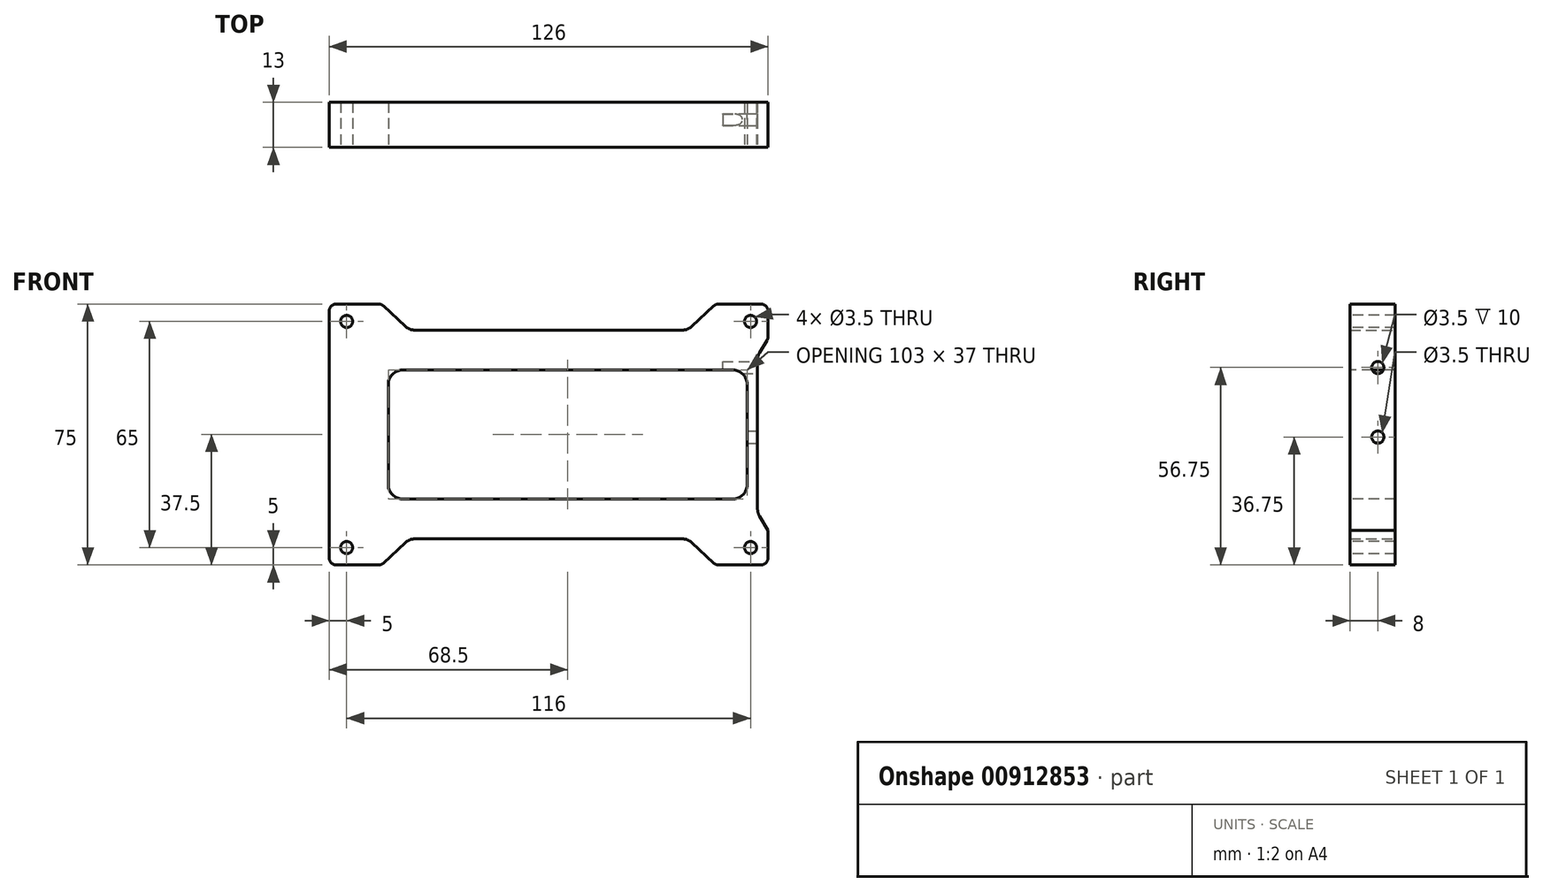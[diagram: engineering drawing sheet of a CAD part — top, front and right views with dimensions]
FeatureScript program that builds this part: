
annotation { "Feature Type Name" : "Feature", "Feature Type Description" : "" }
export const myFeature = defineFeature(function(context is Context, id is Id, definition is map)
    precondition{}
    {
        {
            var Q0;
            Q0=qCreatedBy(makeId("Front.planeOp"),FACE);
            var sketch = newSketch(context, id + "F0", { "sketchPlane" : qUnion([Q0])});
            skLineSegment(sketch, "E0.bottom", {"start": v(0, 0) * mm, "end": v(15, 0) * mm});
            skLineSegment(sketch, "E0.top", {"start": v(0, 75) * mm, "end": v(15, 75) * mm});
            skLineSegment(sketch, "E0.left", {"start": v(0, 0) * mm, "end": v(0, 75) * mm});
            skLineSegment(sketch, "E0.right", {"start": v(126, 0) * mm, "end": v(126, 75) * mm});
            skLineSegment(sketch, "E1", {"start": v(23, 67.5) * mm, "end": v(103, 67.5) * mm});
            skLineSegment(sketch, "E2", {"start": v(23, 7.5) * mm, "end": v(103, 7.5) * mm});
            skLineSegment(sketch, "E3", {"start": v(23, 7.5) * mm, "end": v(15, 0) * mm});
            skLineSegment(sketch, "E4", {"start": v(103, 7.5) * mm, "end": v(111, 0) * mm});
            skLineSegment(sketch, "E5", {"start": v(23, 67.5) * mm, "end": v(15, 75) * mm});
            skLineSegment(sketch, "E6", {"start": v(103, 67.5) * mm, "end": v(111, 75) * mm});
            skLineSegment(sketch, "E7.trimOffspring", {"start": v(111, 75) * mm, "end": v(126, 75) * mm});
            skLineSegment(sketch, "E8.trimOffspring", {"start": v(111, 0) * mm, "end": v(126, 0) * mm});
            skSolve(sketch);
        }
        {
            var Q0;
            Q0 = qSketchRegion(id + "F0", true);
            extrude(context, id + "F1", {"entities" : qUnion([Q0]), "depth" : 13 * mm, "offsetDistance" : 25 * mm});
        }
        {
            var Q0;
            Q0=makeQuery(id+"F1.opExtrude","CAP_FACE",FACE,{"disambiguationData":[OSD([sQuery(id+"F0.wireOp",EDGE,"E0.bottom"),sQuery(id+"F0.wireOp",EDGE,"E0.top"),sQuery(id+"F0.wireOp",EDGE,"E0.left"),sQuery(id+"F0.wireOp",EDGE,"E0.right"),sQuery(id+"F0.wireOp",EDGE,"E1"),sQuery(id+"F0.wireOp",EDGE,"E2"),sQuery(id+"F0.wireOp",EDGE,"E3"),sQuery(id+"F0.wireOp",EDGE,"E4"),sQuery(id+"F0.wireOp",EDGE,"E5"),sQuery(id+"F0.wireOp",EDGE,"E6"),sQuery(id+"F0.wireOp",EDGE,"E7.trimOffspring"),sQuery(id+"F0.wireOp",EDGE,"E8.trimOffspring")])],"isStart":false});
            var sketch = newSketch(context, id + "F2", { "sketchPlane" : qUnion([Q0])});
            skLineSegment(sketch, "E9.bottom", {"start": v(21, 56) * mm, "end": v(116, 56) * mm});
            skLineSegment(sketch, "E9.top", {"start": v(21, 19) * mm, "end": v(116, 19) * mm});
            skLineSegment(sketch, "E9.left", {"start": v(17, 52) * mm, "end": v(17, 23) * mm});
            skLineSegment(sketch, "E9.right", {"start": v(120, 52) * mm, "end": v(120, 23) * mm});
            skPoint(sketch, "E10.visualSharp", {"position": v(17, 56) * mm});
            skArc(sketch, "E10.filletArc", {"start": v(21, 56) * mm, "mid": v(18.17, 54.83) * mm, "end": v(17, 52) * mm});
            skPoint(sketch, "E11.visualSharp", {"position": v(120, 56) * mm});
            skArc(sketch, "E11.filletArc", {"start": v(120, 52) * mm, "mid": v(118.83, 54.83) * mm, "end": v(116, 56) * mm});
            skPoint(sketch, "E12.visualSharp", {"position": v(120, 19) * mm});
            skArc(sketch, "E12.filletArc", {"start": v(116, 19) * mm, "mid": v(118.83, 20.17) * mm, "end": v(120, 23) * mm});
            skPoint(sketch, "E13.visualSharp", {"position": v(17, 19) * mm});
            skArc(sketch, "E13.filletArc", {"start": v(17, 23) * mm, "mid": v(18.17, 20.17) * mm, "end": v(21, 19) * mm});
            skSolve(sketch);
        }
        {
            var Q0;
            Q0 = qSketchRegion(id + "F2", true);
            extrude(context, id + "F3", {"entities" : qUnion([Q0]), "operationType" : NewBodyOperationType.REMOVE, "oppositeDirection" : true, "depth" : 25 * mm, "offsetDistance" : 25 * mm});
        }
        {
            var Q0;
            Q0=makeQuery(id+"F1.opExtrude","CAP_FACE",FACE,{"disambiguationData":[OSD([sQuery(id+"F0.wireOp",EDGE,"E0.bottom"),sQuery(id+"F0.wireOp",EDGE,"E0.top"),sQuery(id+"F0.wireOp",EDGE,"E0.left"),sQuery(id+"F0.wireOp",EDGE,"E0.right"),sQuery(id+"F0.wireOp",EDGE,"E1"),sQuery(id+"F0.wireOp",EDGE,"E2"),sQuery(id+"F0.wireOp",EDGE,"E3"),sQuery(id+"F0.wireOp",EDGE,"E4"),sQuery(id+"F0.wireOp",EDGE,"E5"),sQuery(id+"F0.wireOp",EDGE,"E6"),sQuery(id+"F0.wireOp",EDGE,"E7.trimOffspring"),sQuery(id+"F0.wireOp",EDGE,"E8.trimOffspring")])],"isStart":false});
            var sketch = newSketch(context, id + "F4", { "sketchPlane" : qUnion([Q0])});
            skLineSegment(sketch, "E14", {"start": v(123, 60) * mm, "end": v(123, 15) * mm});
            skLineSegment(sketch, "E15", {"start": v(123, 60) * mm, "end": v(126, 65) * mm});
            skLineSegment(sketch, "E16", {"start": v(123, 15) * mm, "end": v(126, 10) * mm});
            skLineSegment(sketch, "E17", {"start": v(126, 65) * mm, "end": v(126, 10) * mm});
            skSolve(sketch);
        }
        {
            var Q0;
            Q0 = qSketchRegion(id + "F4", true);
            extrude(context, id + "F5", {"entities" : qUnion([Q0]), "operationType" : NewBodyOperationType.REMOVE, "oppositeDirection" : true, "depth" : 25 * mm, "offsetDistance" : 25 * mm});
        }
        {
            var Q0;
            Q0=makeQuery(id+"F5.boolean.opBoolean","COPY",FACE,{"derivedFrom":makeQuery(id+"F5.opExtrude","SWEPT_FACE",FACE,{"disambiguationData":[OSD([sQuery(id+"F4.wireOp",EDGE,"E14")])]})});
            var sketch = newSketch(context, id + "F6", { "sketchPlane" : qUnion([Q0])});
            skCircle(sketch, "E18", {"center": v(-5, 36.75) * mm, "radius": 1.75 * mm});
            skCircle(sketch, "E19", {"center": v(-5, 56.75) * mm, "radius": 1.75 * mm});
            skSolve(sketch);
        }
        {
            var Q0;
            Q0 = qSketchRegion(id + "F6", true);
            extrude(context, id + "F7", {"entities" : qUnion([Q0]), "operationType" : NewBodyOperationType.REMOVE, "oppositeDirection" : true, "depth" : 10 * mm, "offsetDistance" : 25 * mm});
        }
        {
            var Q0;
            Q0=makeQuery(id+"F1.opExtrude","CAP_FACE",FACE,{"disambiguationData":[OSD([sQuery(id+"F0.wireOp",EDGE,"E0.bottom"),sQuery(id+"F0.wireOp",EDGE,"E0.top"),sQuery(id+"F0.wireOp",EDGE,"E0.left"),sQuery(id+"F0.wireOp",EDGE,"E0.right"),sQuery(id+"F0.wireOp",EDGE,"E1"),sQuery(id+"F0.wireOp",EDGE,"E2"),sQuery(id+"F0.wireOp",EDGE,"E3"),sQuery(id+"F0.wireOp",EDGE,"E4"),sQuery(id+"F0.wireOp",EDGE,"E5"),sQuery(id+"F0.wireOp",EDGE,"E6"),sQuery(id+"F0.wireOp",EDGE,"E7.trimOffspring"),sQuery(id+"F0.wireOp",EDGE,"E8.trimOffspring")])],"isStart":false});
            var sketch = newSketch(context, id + "F8", { "sketchPlane" : qUnion([Q0])});
            skCircle(sketch, "E20", {"center": v(5, 70) * mm, "radius": 1.75 * mm});
            skCircle(sketch, "E21", {"center": v(5, 5) * mm, "radius": 1.75 * mm});
            skCircle(sketch, "E22", {"center": v(121, 5) * mm, "radius": 1.75 * mm});
            skCircle(sketch, "E23", {"center": v(121, 70) * mm, "radius": 1.75 * mm});
            skSolve(sketch);
        }
        {
            var Q0;
            Q0 = qSketchRegion(id + "F8", true);
            extrude(context, id + "F9", {"entities" : qUnion([Q0]), "operationType" : NewBodyOperationType.REMOVE, "oppositeDirection" : true, "depth" : 25 * mm, "offsetDistance" : 25 * mm});
        }
        {
            var Q0;
            Q0=makeQuery(id+"F1.opExtrude","SWEPT_EDGE",EDGE,{"disambiguationData":[OSD([sQuery(id+"F0.wireOp",EDGE,"E2"),sQuery(id+"F0.wireOp",EDGE,"E3")])]});
            var Q1;
            Q1=makeQuery(id+"F1.opExtrude","SWEPT_EDGE",EDGE,{"disambiguationData":[OSD([sQuery(id+"F0.wireOp",EDGE,"E2"),sQuery(id+"F0.wireOp",EDGE,"E4")])]});
            var Q2;
            Q2=makeQuery(id+"F5.boolean.opBoolean","COPY",EDGE,{"derivedFrom":makeQuery(id+"F5.opExtrude","SWEPT_EDGE",EDGE,{"disambiguationData":[OSD([sQuery(id+"F4.wireOp",EDGE,"E14"),sQuery(id+"F4.wireOp",EDGE,"E16")])]})});
            var Q3;
            Q3=makeQuery(id+"F5.boolean.opBoolean","COPY",EDGE,{"derivedFrom":makeQuery(id+"F5.opExtrude","SWEPT_EDGE",EDGE,{"disambiguationData":[OSD([sQuery(id+"F4.wireOp",EDGE,"E14"),sQuery(id+"F4.wireOp",EDGE,"E15")])]})});
            var Q4;
            Q4=makeQuery(id+"F1.opExtrude","SWEPT_EDGE",EDGE,{"disambiguationData":[OSD([sQuery(id+"F0.wireOp",EDGE,"E1"),sQuery(id+"F0.wireOp",EDGE,"E6")])]});
            var Q5;
            Q5=makeQuery(id+"F1.opExtrude","SWEPT_EDGE",EDGE,{"disambiguationData":[OSD([sQuery(id+"F0.wireOp",EDGE,"E1"),sQuery(id+"F0.wireOp",EDGE,"E5")])]});
            fillet(context, id + "F10", {"entities" : qUnion([Q0, Q1, Q2, Q3, Q4, Q5]), "radius" : 4 * mm, "tangentPropagation" : true, "allowEdgeOverflow" : false});
        }
        {
            var Q0;
            Q0=makeQuery(id+"F1.opExtrude","SWEPT_EDGE",EDGE,{"disambiguationData":[OSD([sQuery(id+"F0.wireOp",EDGE,"E0.top"),sQuery(id+"F0.wireOp",EDGE,"E0.left")])]});
            var Q1;
            Q1=makeQuery(id+"F1.opExtrude","SWEPT_EDGE",EDGE,{"disambiguationData":[OSD([sQuery(id+"F0.wireOp",EDGE,"E0.bottom"),sQuery(id+"F0.wireOp",EDGE,"E0.left")])]});
            var Q2;
            Q2=makeQuery(id+"F1.opExtrude","SWEPT_EDGE",EDGE,{"disambiguationData":[OSD([sQuery(id+"F0.wireOp",EDGE,"E0.bottom"),sQuery(id+"F0.wireOp",EDGE,"E3")])]});
            var Q3;
            Q3=makeQuery(id+"F1.opExtrude","SWEPT_EDGE",EDGE,{"disambiguationData":[OSD([sQuery(id+"F0.wireOp",EDGE,"E4"),sQuery(id+"F0.wireOp",EDGE,"E8.trimOffspring")])]});
            var Q4;
            Q4=makeQuery(id+"F1.opExtrude","SWEPT_EDGE",EDGE,{"disambiguationData":[OSD([sQuery(id+"F0.wireOp",EDGE,"E0.right"),sQuery(id+"F0.wireOp",EDGE,"E8.trimOffspring")])]});
            var Q5;
            Q5=makeQuery(id+"F5.boolean.opBoolean","COPY",EDGE,{"derivedFrom":makeQuery(id+"F5.opExtrude","SWEPT_EDGE",EDGE,{"disambiguationData":[OSD([sQuery(id+"F0.wireOp",EDGE,"E0.right"),sQuery(id+"F4.wireOp",EDGE,"E16"),sQuery(id+"F4.wireOp",EDGE,"E17")])]})});
            var Q6;
            Q6=makeQuery(id+"F5.boolean.opBoolean","COPY",EDGE,{"derivedFrom":makeQuery(id+"F5.opExtrude","SWEPT_EDGE",EDGE,{"disambiguationData":[OSD([sQuery(id+"F0.wireOp",EDGE,"E0.right"),sQuery(id+"F4.wireOp",EDGE,"E15"),sQuery(id+"F4.wireOp",EDGE,"E17")])]})});
            var Q7;
            Q7=makeQuery(id+"F1.opExtrude","SWEPT_EDGE",EDGE,{"disambiguationData":[OSD([sQuery(id+"F0.wireOp",EDGE,"E0.right"),sQuery(id+"F0.wireOp",EDGE,"E7.trimOffspring")])]});
            var Q8;
            Q8=makeQuery(id+"F1.opExtrude","SWEPT_EDGE",EDGE,{"disambiguationData":[OSD([sQuery(id+"F0.wireOp",EDGE,"E6"),sQuery(id+"F0.wireOp",EDGE,"E7.trimOffspring")])]});
            var Q9;
            Q9=makeQuery(id+"F1.opExtrude","SWEPT_EDGE",EDGE,{"disambiguationData":[OSD([sQuery(id+"F0.wireOp",EDGE,"E0.top"),sQuery(id+"F0.wireOp",EDGE,"E5")])]});
            fillet(context, id + "F11", {"entities" : qUnion([Q0, Q1, Q2, Q3, Q4, Q5, Q6, Q7, Q8, Q9]), "radius" : 2 * mm, "tangentPropagation" : true, "allowEdgeOverflow" : false});
        }
    });
